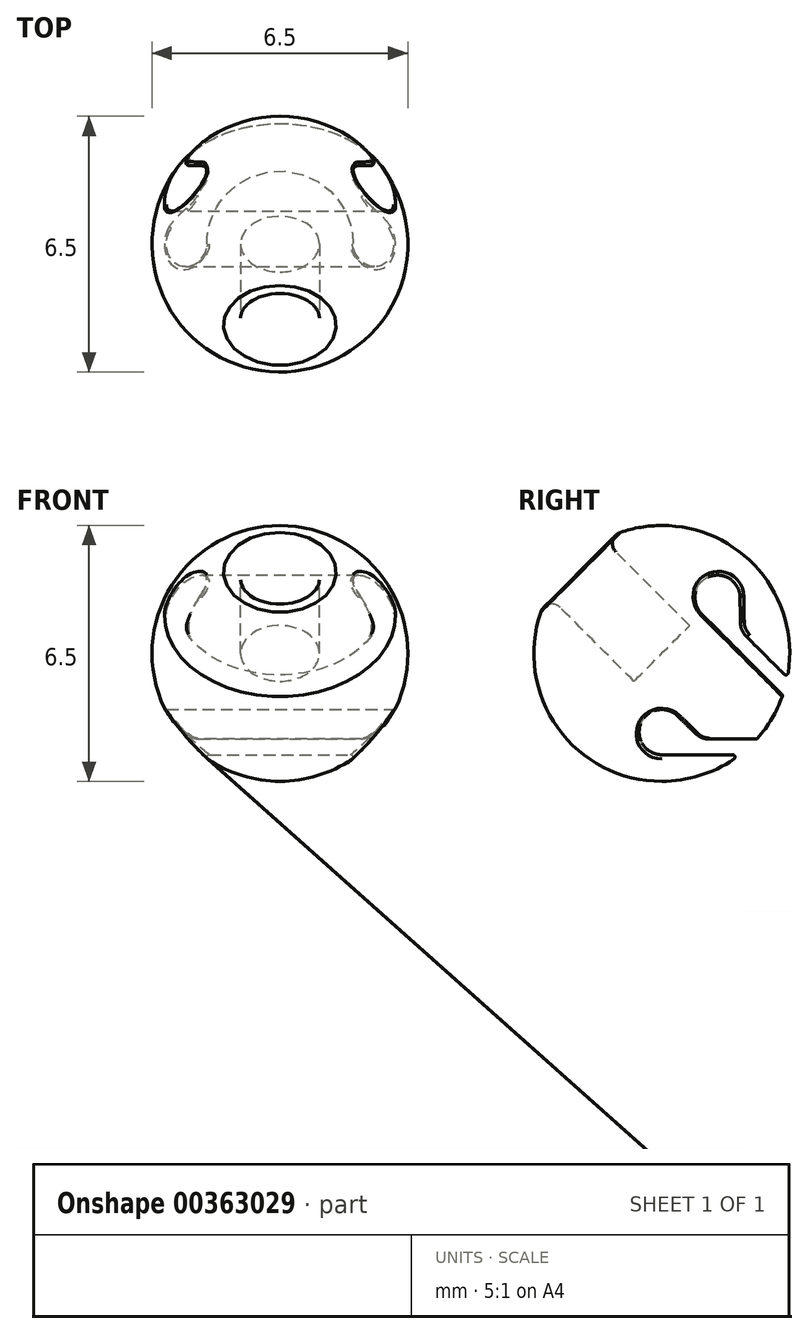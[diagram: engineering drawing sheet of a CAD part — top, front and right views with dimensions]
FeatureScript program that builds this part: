
annotation { "Feature Type Name" : "Feature", "Feature Type Description" : "" }
export const myFeature = defineFeature(function(context is Context, id is Id, definition is map)
    precondition{}
    {
        {
            var Q0;
            Q0=qCreatedBy(makeId("Front.planeOp"),FACE);
            var sketch = newSketch(context, id + "F0", { "sketchPlane" : qUnion([Q0])});
            skArc(sketch, "E0", {"start": v(0, 3.25) * mm, "mid": v(3.25, 0) * mm, "end": v(0, -3.25) * mm});
            skLineSegment(sketch, "E1", {"start": v(0, 3.25) * mm, "end": v(0, -3.25) * mm});
            skSolve(sketch);
        }
        {
            var Q0;
            Q0=qCreatedBy(makeId("Front.planeOp"),FACE);
            var sketch = newSketch(context, id + "F1", { "sketchPlane" : qUnion([Q0])});
            skLineSegment(sketch, "E2", {"start": v(0, -6.34) * mm, "end": v(0, 6.68) * mm, "construction": true});
            skSolve(sketch);
        }
        {
            var Q0;
            Q0 = qSketchRegion(id + "F0", true);
            var Q1;
            Q1=sQuery(id+"F1.wireOp",EDGE,"E2");
            revolve(context, id + "F2", {"entities" : qUnion([Q0]), "axis" : qUnion([Q1]), "revolveType" : RevolveType.FULL});
        }
        {
            var Q0;
            Q0=qCreatedBy(makeId("Front.planeOp"),FACE);
            var Q1;
            Q1=qCreatedBy(makeId("Top.planeOp"),FACE);
            cPlane(context, id + "F3", {"entities" : qUnion([Q0, Q1]), "cplaneType" : CPlaneType.MID_PLANE, "offset" : 25 * mm, "flipAlignment" : true, "width" : 150 * mm, "height" : 150 * mm});
        }
        {
            var Q0;
            Q0=qCreatedBy(id+"F3.planeOp",FACE);
            cPlane(context, id + "F4", {"entities" : qUnion([Q0]), "cplaneType" : CPlaneType.OFFSET, "offset" : 4 * mm, "width" : 150 * mm, "height" : 150 * mm});
        }
        {
            var Q0;
            Q0=qCreatedBy(id+"F4.planeOp",FACE);
            var sketch = newSketch(context, id + "F5", { "sketchPlane" : qUnion([Q0])});
            skCircle(sketch, "E3", {"center": v(0, 0) * mm, "radius": 1 * mm});
            skSolve(sketch);
        }
        {
            var Q0;
            Q0 = qSketchRegion(id + "F5", true);
            extrude(context, id + "F6", {"entities" : qUnion([Q0]), "operationType" : NewBodyOperationType.REMOVE, "oppositeDirection" : true, "depth" : 4 * mm});
        }
        {
            var Q0;
            Q0=qCreatedBy(makeId("Right.planeOp"),FACE);
            var sketch = newSketch(context, id + "F7", { "sketchPlane" : qUnion([Q0])});
            skCircle(sketch, "E4", {"center": v(0, -2) * mm, "radius": 0.57 * mm, "construction": true});
            skLineSegment(sketch, "E5", {"start": v(0, -2.58) * mm, "end": v(3.89, -2.57) * mm});
            skLineSegment(sketch, "E6", {"start": v(3.89, -2.57) * mm, "end": v(3.89, -2.17) * mm});
            skLineSegment(sketch, "E7", {"start": v(3.89, -2.17) * mm, "end": v(1.2, -2.17) * mm});
            skLineSegment(sketch, "E8", {"start": v(0.85, -2.03) * mm, "end": v(0.4, -1.59) * mm});
            skArc(sketch, "E9", {"start": v(0.4, -1.59) * mm, "mid": v(-0.53, -1.78) * mm, "end": v(0, -2.58) * mm});
            skPoint(sketch, "E10.visualSharp", {"position": v(1, -2.17) * mm});
            skArc(sketch, "E10.filletArc", {"start": v(0.85, -2.03) * mm, "mid": v(1.02, -2.14) * mm, "end": v(1.2, -2.17) * mm});
            skLineSegment(sketch, "E11", {"start": v(0, 0) * mm, "end": v(6.95, -6.95) * mm, "construction": true});
            skLineSegment(sketch, "E12", {"start": v(0, 0) * mm, "end": v(1.41, 1.41) * mm, "construction": true});
            skCircle(sketch, "E13", {"center": v(1.41, 1.41) * mm, "radius": 0.57 * mm, "construction": true});
            skLineSegment(sketch, "E14", {"start": v(1, 1) * mm, "end": v(4.03, -2.01) * mm});
            skLineSegment(sketch, "E15", {"start": v(4.03, -2.01) * mm, "end": v(4.3, -1.73) * mm});
            skLineSegment(sketch, "E16", {"start": v(4.3, -1.73) * mm, "end": v(2.14, 0.44) * mm});
            skLineSegment(sketch, "E17", {"start": v(2, 0.79) * mm, "end": v(1.99, 1.42) * mm});
            skArc(sketch, "E18", {"start": v(1.99, 1.42) * mm, "mid": v(1.2, 1.94) * mm, "end": v(1, 1) * mm});
            skLineSegment(sketch, "E19", {"start": v(2, 0.58) * mm, "end": v(0.7, -0.7) * mm, "construction": true});
            skPoint(sketch, "E20.visualSharp", {"position": v(2, 0.58) * mm});
            skArc(sketch, "E20.filletArc", {"start": v(2, 0.79) * mm, "mid": v(2.03, 0.6) * mm, "end": v(2.14, 0.44) * mm});
            skSolve(sketch);
        }
        {
            var Q0;
            Q0=makeQuery(id+"F7.imprint","IMPRINT",FACE,{"disambiguationData":[TD([[makeQuery(id+"F7.imprint","IMPRINT",EDGE,{"derivedFrom":sQuery(id+"F7.wireOp",EDGE,"E5")}),1.0]])]});
            var Q1;
            Q1=makeQuery(id+"F7.imprint","IMPRINT",FACE,{"disambiguationData":[TD([[makeQuery(id+"F7.imprint","IMPRINT",EDGE,{"derivedFrom":sQuery(id+"F7.wireOp",EDGE,"E14")}),1.0]])]});
            extrude(context, id + "F8", {"entities" : qUnion([Q0, Q1]), "operationType" : NewBodyOperationType.REMOVE, "endBound" : BoundingType.SYMMETRIC, "oppositeDirection" : true, "depth" : 25 * mm});
        }
        {
            var Q0;
            Q0=makeQuery(id+"F6.boolean.opBoolean","INTERSECT",EDGE,{"derivedFrom":[makeQuery(id+"F2.opRevolve","SWEPT_FACE",FACE,{"disambiguationData":[OSD([sQuery(id+"F0.wireOp",EDGE,"E0")])]}),makeQuery(id+"F6.opExtrude","SWEPT_FACE",FACE,{"disambiguationData":[OSD([sQuery(id+"F5.wireOp",EDGE,"E3")])]})]});
            fillet(context, id + "F9", {"entities" : qUnion([Q0]), "radius" : 0.3 * mm, "tangentPropagation" : true, "allowEdgeOverflow" : false});
        }
        {
            var Q0;
            Q0=makeQuery(id+"F8.boolean.opBoolean","INTERSECT",EDGE,{"derivedFrom":[makeQuery(id+"F2.opRevolve","SWEPT_FACE",FACE,{"disambiguationData":[OSD([sQuery(id+"F0.wireOp",EDGE,"E0")])]}),makeQuery(id+"F8.opExtrude","SWEPT_FACE",FACE,{"disambiguationData":[OSD([sQuery(id+"F7.wireOp",EDGE,"E16")])]})]});
            var Q1;
            Q1=makeQuery(id+"F8.boolean.opBoolean","INTERSECT",EDGE,{"derivedFrom":[makeQuery(id+"F2.opRevolve","SWEPT_FACE",FACE,{"disambiguationData":[OSD([sQuery(id+"F0.wireOp",EDGE,"E0")])]}),makeQuery(id+"F8.opExtrude","SWEPT_FACE",FACE,{"disambiguationData":[OSD([sQuery(id+"F7.wireOp",EDGE,"E5")])]})]});
            var Q2;
            Q2=makeQuery(id+"F8.boolean.opBoolean","INTERSECT",EDGE,{"disambiguationData":[OD(1.0)],"derivedFrom":[makeQuery(id+"F2.opRevolve","SWEPT_FACE",FACE,{"disambiguationData":[OSD([sQuery(id+"F0.wireOp",EDGE,"E0")])]}),makeQuery(id+"F8.opExtrude","SWEPT_FACE",FACE,{"disambiguationData":[OSD([sQuery(id+"F7.wireOp",EDGE,"E9")])]})]});
            var Q3;
            Q3=makeQuery(id+"F8.boolean.opBoolean","INTERSECT",EDGE,{"disambiguationData":[OD(0.0)],"derivedFrom":[makeQuery(id+"F2.opRevolve","SWEPT_FACE",FACE,{"disambiguationData":[OSD([sQuery(id+"F0.wireOp",EDGE,"E0")])]}),makeQuery(id+"F8.opExtrude","SWEPT_FACE",FACE,{"disambiguationData":[OSD([sQuery(id+"F7.wireOp",EDGE,"E9")])]})]});
            var Q4;
            Q4=makeQuery(id+"F8.boolean.opBoolean","INTERSECT",EDGE,{"disambiguationData":[OD(0.0)],"derivedFrom":[makeQuery(id+"F2.opRevolve","SWEPT_FACE",FACE,{"disambiguationData":[OSD([sQuery(id+"F0.wireOp",EDGE,"E0")])]}),makeQuery(id+"F8.opExtrude","SWEPT_FACE",FACE,{"disambiguationData":[OSD([sQuery(id+"F7.wireOp",EDGE,"E8")])]})]});
            var Q5;
            Q5=makeQuery(id+"F8.boolean.opBoolean","INTERSECT",EDGE,{"disambiguationData":[OD(0.0)],"derivedFrom":[makeQuery(id+"F2.opRevolve","SWEPT_FACE",FACE,{"disambiguationData":[OSD([sQuery(id+"F0.wireOp",EDGE,"E0")])]}),makeQuery(id+"F8.opExtrude","SWEPT_FACE",FACE,{"disambiguationData":[OSD([sQuery(id+"F7.wireOp",EDGE,"E10.filletArc")])]})]});
            var Q6;
            Q6=makeQuery(id+"F8.boolean.opBoolean","INTERSECT",EDGE,{"derivedFrom":[makeQuery(id+"F2.opRevolve","SWEPT_FACE",FACE,{"disambiguationData":[OSD([sQuery(id+"F0.wireOp",EDGE,"E0")])]}),makeQuery(id+"F8.opExtrude","SWEPT_FACE",FACE,{"disambiguationData":[OSD([sQuery(id+"F7.wireOp",EDGE,"E7")])]})]});
            var Q7;
            Q7=makeQuery(id+"F8.boolean.opBoolean","INTERSECT",EDGE,{"disambiguationData":[OD(0.0)],"derivedFrom":[makeQuery(id+"F2.opRevolve","SWEPT_FACE",FACE,{"disambiguationData":[OSD([sQuery(id+"F0.wireOp",EDGE,"E0")])]}),makeQuery(id+"F8.opExtrude","SWEPT_FACE",FACE,{"disambiguationData":[OSD([sQuery(id+"F7.wireOp",EDGE,"E18")])]})]});
            var Q8;
            Q8=makeQuery(id+"F8.boolean.opBoolean","INTERSECT",EDGE,{"disambiguationData":[OD(0.0)],"derivedFrom":[makeQuery(id+"F2.opRevolve","SWEPT_FACE",FACE,{"disambiguationData":[OSD([sQuery(id+"F0.wireOp",EDGE,"E0")])]}),makeQuery(id+"F8.opExtrude","SWEPT_FACE",FACE,{"disambiguationData":[OSD([sQuery(id+"F7.wireOp",EDGE,"E17")])]})]});
            var Q9;
            Q9=makeQuery(id+"F8.boolean.opBoolean","INTERSECT",EDGE,{"disambiguationData":[OD(0.0)],"derivedFrom":[makeQuery(id+"F2.opRevolve","SWEPT_FACE",FACE,{"disambiguationData":[OSD([sQuery(id+"F0.wireOp",EDGE,"E0")])]}),makeQuery(id+"F8.opExtrude","SWEPT_FACE",FACE,{"disambiguationData":[OSD([sQuery(id+"F7.wireOp",EDGE,"E20.filletArc")])]})]});
            var Q10;
            Q10=makeQuery(id+"F8.boolean.opBoolean","INTERSECT",EDGE,{"disambiguationData":[OD(1.0)],"derivedFrom":[makeQuery(id+"F2.opRevolve","SWEPT_FACE",FACE,{"disambiguationData":[OSD([sQuery(id+"F0.wireOp",EDGE,"E0")])]}),makeQuery(id+"F8.opExtrude","SWEPT_FACE",FACE,{"disambiguationData":[OSD([sQuery(id+"F7.wireOp",EDGE,"E17")])]})]});
            var Q11;
            Q11=makeQuery(id+"F8.boolean.opBoolean","INTERSECT",EDGE,{"disambiguationData":[OD(1.0)],"derivedFrom":[makeQuery(id+"F2.opRevolve","SWEPT_FACE",FACE,{"disambiguationData":[OSD([sQuery(id+"F0.wireOp",EDGE,"E0")])]}),makeQuery(id+"F8.opExtrude","SWEPT_FACE",FACE,{"disambiguationData":[OSD([sQuery(id+"F7.wireOp",EDGE,"E20.filletArc")])]})]});
            var Q12;
            Q12=makeQuery(id+"F8.boolean.opBoolean","INTERSECT",EDGE,{"disambiguationData":[OD(1.0)],"derivedFrom":[makeQuery(id+"F2.opRevolve","SWEPT_FACE",FACE,{"disambiguationData":[OSD([sQuery(id+"F0.wireOp",EDGE,"E0")])]}),makeQuery(id+"F8.opExtrude","SWEPT_FACE",FACE,{"disambiguationData":[OSD([sQuery(id+"F7.wireOp",EDGE,"E18")])]})]});
            var Q13;
            Q13=makeQuery(id+"F8.boolean.opBoolean","INTERSECT",EDGE,{"derivedFrom":[makeQuery(id+"F2.opRevolve","SWEPT_FACE",FACE,{"disambiguationData":[OSD([sQuery(id+"F0.wireOp",EDGE,"E0")])]}),makeQuery(id+"F8.opExtrude","SWEPT_FACE",FACE,{"disambiguationData":[OSD([sQuery(id+"F7.wireOp",EDGE,"E14")])]})]});
            fillet(context, id + "F10", {"entities" : qUnion([Q0, Q1, Q2, Q3, Q4, Q5, Q6, Q7, Q8, Q9, Q10, Q11, Q12, Q13]), "radius" : 0.06 * mm, "tangentPropagation" : true, "allowEdgeOverflow" : false});
        }
    });
